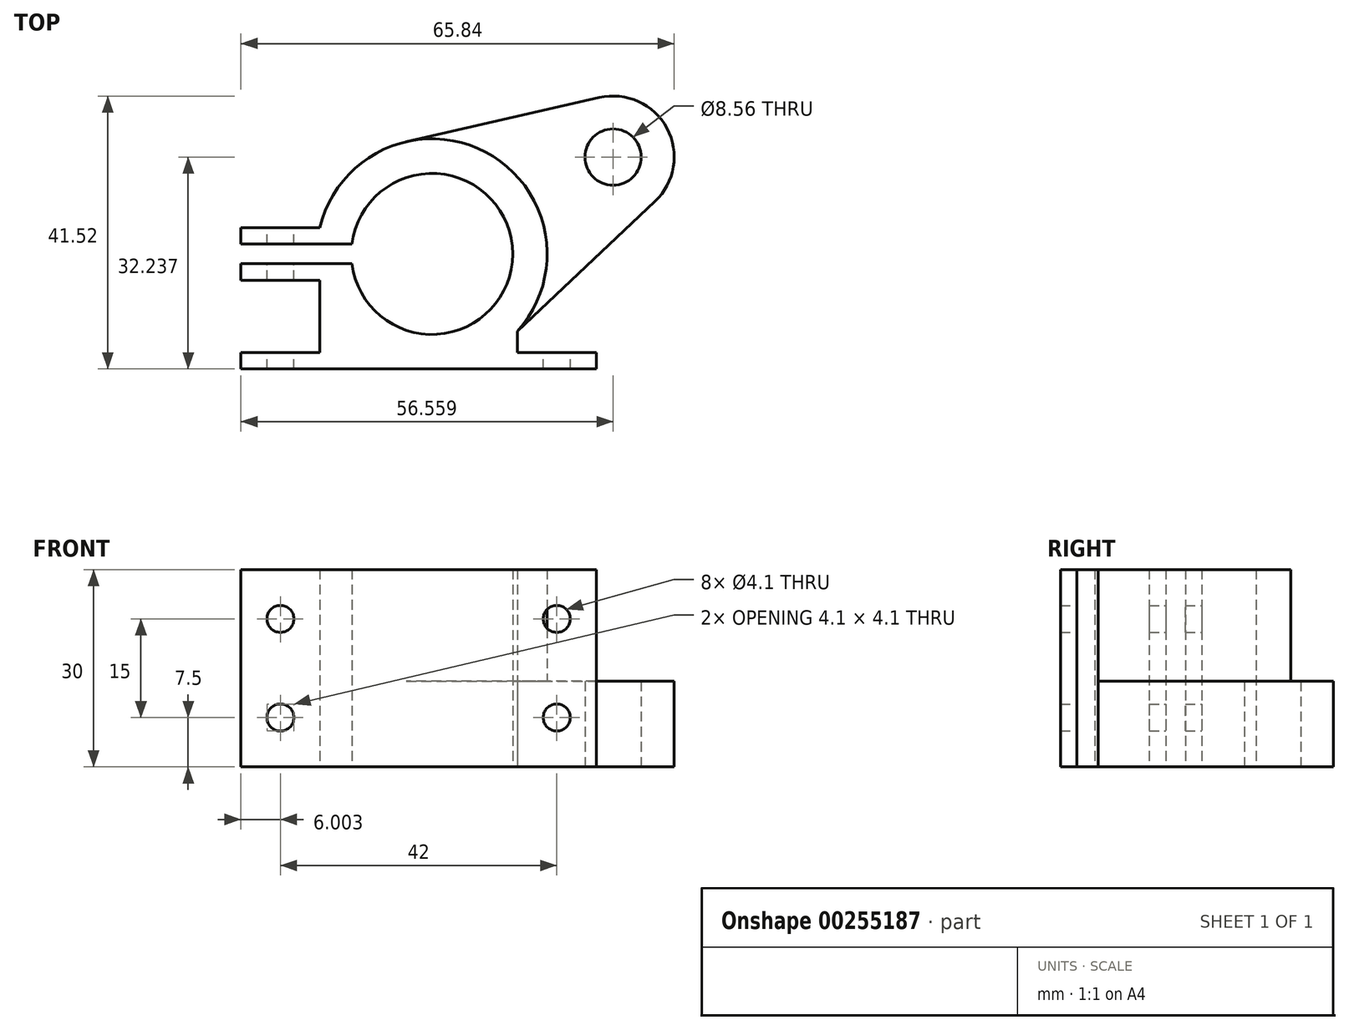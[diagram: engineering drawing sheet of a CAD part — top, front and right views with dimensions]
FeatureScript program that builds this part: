
annotation { "Feature Type Name" : "Feature", "Feature Type Description" : "" }
export const myFeature = defineFeature(function(context is Context, id is Id, definition is map)
    precondition{}
    {
        {
            var Q0;
            Q0=qCreatedBy(makeId("Top.planeOp"),FACE);
            var sketch = newSketch(context, id + "F0", { "sketchPlane" : qUnion([Q0])});
            skArc(sketch, "E0", {"start": v(-12.16, -1.5) * mm, "mid": v(12.25, 0) * mm, "end": v(-12.16, 1.5) * mm});
            skArc(sketch, "E1", {"start": v(12.96, -11.76) * mm, "mid": v(8.14, 15.5) * mm, "end": v(-17.04, 4) * mm});
            skLineSegment(sketch, "E2", {"start": v(12.96, -17.5) * mm, "end": v(-17.04, -17.5) * mm});
            skLineSegment(sketch, "E3", {"start": v(-29.04, -1.5) * mm, "end": v(-12.16, -1.5) * mm});
            skLineSegment(sketch, "E4", {"start": v(-12.16, 1.5) * mm, "end": v(-29.04, 1.5) * mm});
            skLineSegment(sketch, "E5", {"start": v(-29.04, 1.5) * mm, "end": v(-29.04, 4) * mm});
            skLineSegment(sketch, "E6", {"start": v(-29.04, 4) * mm, "end": v(-17.04, 4) * mm});
            skLineSegment(sketch, "E7", {"start": v(-29.04, -1.5) * mm, "end": v(-29.04, -4) * mm});
            skLineSegment(sketch, "E8", {"start": v(-29.04, -4) * mm, "end": v(-17.04, -4) * mm});
            skLineSegment(sketch, "E9", {"start": v(-17.04, -4) * mm, "end": v(-17.04, -17.5) * mm});
            skLineSegment(sketch, "E10", {"start": v(12.96, -17.5) * mm, "end": v(12.96, -11.76) * mm});
            skLineSegment(sketch, "E11", {"start": v(0, 0) * mm, "end": v(-42.44, 0) * mm, "construction": true});
            skLineSegment(sketch, "E12", {"start": v(-17.04, -17.5) * mm, "end": v(-29.04, -17.5) * mm});
            skLineSegment(sketch, "E13", {"start": v(-29.04, -17.5) * mm, "end": v(-29.04, -15) * mm});
            skLineSegment(sketch, "E14", {"start": v(-29.04, -15) * mm, "end": v(-17.04, -15) * mm});
            skLineSegment(sketch, "E15", {"start": v(12.96, -17.5) * mm, "end": v(24.96, -17.5) * mm});
            skLineSegment(sketch, "E16", {"start": v(24.96, -17.5) * mm, "end": v(24.96, -15) * mm});
            skLineSegment(sketch, "E17", {"start": v(24.96, -15) * mm, "end": v(12.96, -15) * mm});
            skLineSegment(sketch, "E18", {"start": v(0, 0) * mm, "end": v(27.52, 14.74) * mm, "construction": true});
            skCircle(sketch, "E19", {"center": v(27.52, 14.74) * mm, "radius": 26.99 * mm, "construction": true});
            skLineSegment(sketch, "E20", {"start": v(0, -12.25) * mm, "end": v(27.52, -12.25) * mm, "construction": true});
            skCircle(sketch, "E21", {"center": v(0, 0) * mm, "radius": 3.97 * mm, "construction": true});
            skCircle(sketch, "E22", {"center": v(27.52, 14.74) * mm, "radius": 4.28 * mm});
            skCircle(sketch, "E23.0", {"center": v(27.52, 14.74) * mm, "radius": 9.28 * mm});
            skLineSegment(sketch, "E24", {"start": v(-3.9, 17.06) * mm, "end": v(25.45, 23.78) * mm});
            skLineSegment(sketch, "E25", {"start": v(33.89, 7.99) * mm, "end": v(12.96, -11.76) * mm});
            skLineSegment(sketch, "E26", {"start": v(24.96, -17.5) * mm, "end": v(43.94, -17.5) * mm, "construction": true});
            skSolve(sketch);
        }
        {
            var Q0;
            {var subQ0=sQuery(id+"F0.wireOp",EDGE,"E12");Q0=makeQuery(id+"F0.imprint","IMPRINT",FACE,{"disambiguationData":[TD([[makeQuery(id+"F0.imprint","IMPRINT",EDGE,{"derivedFrom":subQ0}),-1.0]])]});}
            var Q1;
            {var subQ0=sQuery(id+"F0.wireOp",EDGE,"E15");Q1=makeQuery(id+"F0.imprint","IMPRINT",FACE,{"disambiguationData":[TD([[makeQuery(id+"F0.imprint","IMPRINT",EDGE,{"derivedFrom":subQ0}),1.0]])]});}
            var Q2;
            Q2=makeQuery(id+"F0.imprint","IMPRINT",FACE,{"disambiguationData":[TD([[makeQuery(id+"F0.imprint","IMPRINT",EDGE,{"derivedFrom":sQuery(id+"F0.wireOp",EDGE,"E0")}),-1.0]])]});
            extrude(context, id + "F1", {"entities" : qUnion([Q0, Q1, Q2]), "depth" : 30 * mm});
        }
        {
            var Q0;
            Q0=makeQuery(id+"F1.opExtrude","SWEPT_FACE",FACE,{"disambiguationData":[OSD([sQuery(id+"F0.wireOp",EDGE,"E6")])]});
            var sketch = newSketch(context, id + "F2", { "sketchPlane" : qUnion([Q0])});
            skLineSegment(sketch, "E27", {"start": v(29.04, 15) * mm, "end": v(17.04, 15) * mm, "construction": true});
            skLineSegment(sketch, "E28", {"start": v(23.04, 7.5) * mm, "end": v(23.04, 22.5) * mm, "construction": true});
            skPoint(sketch, "E29", {"position": v(23.04, 15) * mm});
            skSolve(sketch);
        }
        {
            var Q0;
            Q0=sQuery(id+"F2.wireOp",VERTEX,"E28.start");
            var Q1;
            Q1=sQuery(id+"F2.wireOp",VERTEX,"E28.end");
            var Q2;
            Q2=makeQuery(id+"F1.opExtrude","SWEPT_BODY",BODY,{"disambiguationData":[OSD([sQuery(id+"F0.wireOp",EDGE,"E0"),sQuery(id+"F0.wireOp",EDGE,"E1"),sQuery(id+"F0.wireOp",EDGE,"E2"),sQuery(id+"F0.wireOp",EDGE,"E3"),sQuery(id+"F0.wireOp",EDGE,"E4"),sQuery(id+"F0.wireOp",EDGE,"E5"),sQuery(id+"F0.wireOp",EDGE,"E6"),sQuery(id+"F0.wireOp",EDGE,"E7"),sQuery(id+"F0.wireOp",EDGE,"E8"),sQuery(id+"F0.wireOp",EDGE,"E9"),sQuery(id+"F0.wireOp",EDGE,"E10")])]});
            hole(context, id + "F3", {"style" : HoleStyle.SIMPLE, "endStyle" : HoleEndStyle.THROUGH, "holeDiameter" : 4.1 * mm, "tappedDepth" : 12 * mm, "tapClearance" : 3, "locations" : qUnion([Q0, Q1]), "scope" : qUnion([Q2])});
        }
        {
            var Q0;
            Q0=makeQuery(id+"F1.opExtrude","SWEPT_FACE",FACE,{"disambiguationData":[OSD([sQuery(id+"F0.wireOp",EDGE,"E17")])]});
            var sketch = newSketch(context, id + "F4", { "sketchPlane" : qUnion([Q0])});
            skLineSegment(sketch, "E30", {"start": v(-18.96, 0) * mm, "end": v(-18.96, 15) * mm, "construction": true});
            skPoint(sketch, "E31", {"position": v(-18.96, 15) * mm});
            skLineSegment(sketch, "E32", {"start": v(-18.96, 15) * mm, "end": v(-18.96, 30) * mm, "construction": true});
            skPoint(sketch, "E33", {"position": v(-18.96, 7.5) * mm});
            skPoint(sketch, "E34", {"position": v(-18.96, 22.5) * mm});
            skSolve(sketch);
        }
        {
            var Q0;
            Q0=sQuery(id+"F4.wireOp",VERTEX,"E34");
            var Q1;
            Q1=sQuery(id+"F4.wireOp",VERTEX,"E33");
            var Q2;
            Q2=makeQuery(id+"F1.opExtrude","SWEPT_BODY",BODY,{"disambiguationData":[OSD([sQuery(id+"F0.wireOp",EDGE,"E0"),sQuery(id+"F0.wireOp",EDGE,"E1"),sQuery(id+"F0.wireOp",EDGE,"E2"),sQuery(id+"F0.wireOp",EDGE,"E3"),sQuery(id+"F0.wireOp",EDGE,"E4"),sQuery(id+"F0.wireOp",EDGE,"E5"),sQuery(id+"F0.wireOp",EDGE,"E6"),sQuery(id+"F0.wireOp",EDGE,"E7"),sQuery(id+"F0.wireOp",EDGE,"E8"),sQuery(id+"F0.wireOp",EDGE,"E9"),sQuery(id+"F0.wireOp",EDGE,"E10"),sQuery(id+"F0.wireOp",EDGE,"E12"),sQuery(id+"F0.wireOp",EDGE,"E13"),sQuery(id+"F0.wireOp",EDGE,"E14"),sQuery(id+"F0.wireOp",EDGE,"E15"),sQuery(id+"F0.wireOp",EDGE,"E16"),sQuery(id+"F0.wireOp",EDGE,"E17")])]});
            hole(context, id + "F5", {"style" : HoleStyle.SIMPLE, "endStyle" : HoleEndStyle.THROUGH, "holeDiameter" : 4.1 * mm, "tappedDepth" : 12 * mm, "tapClearance" : 3, "locations" : qUnion([Q0, Q1]), "scope" : qUnion([Q2])});
        }
        {
            var Q0;
            {var subQ2=sQuery(id+"F0.wireOp",EDGE,"E24");Q0=makeQuery(id+"F0.imprint","IMPRINT",FACE,{"disambiguationData":[TD([[makeQuery(id+"F0.imprint","IMPRINT",EDGE,{"derivedFrom":subQ2}),-1.0]])]});}
            var Q1;
            Q1=makeQuery(id+"F0.imprint","IMPRINT",FACE,{"disambiguationData":[TD([[makeQuery(id+"F0.imprint","IMPRINT",EDGE,{"derivedFrom":sQuery(id+"F0.wireOp",EDGE,"E22")}),-1.0]])]});
            extrude(context, id + "F6", {"entities" : qUnion([Q0, Q1]), "operationType" : NewBodyOperationType.ADD, "depth" : 13 * mm});
        }
    });
